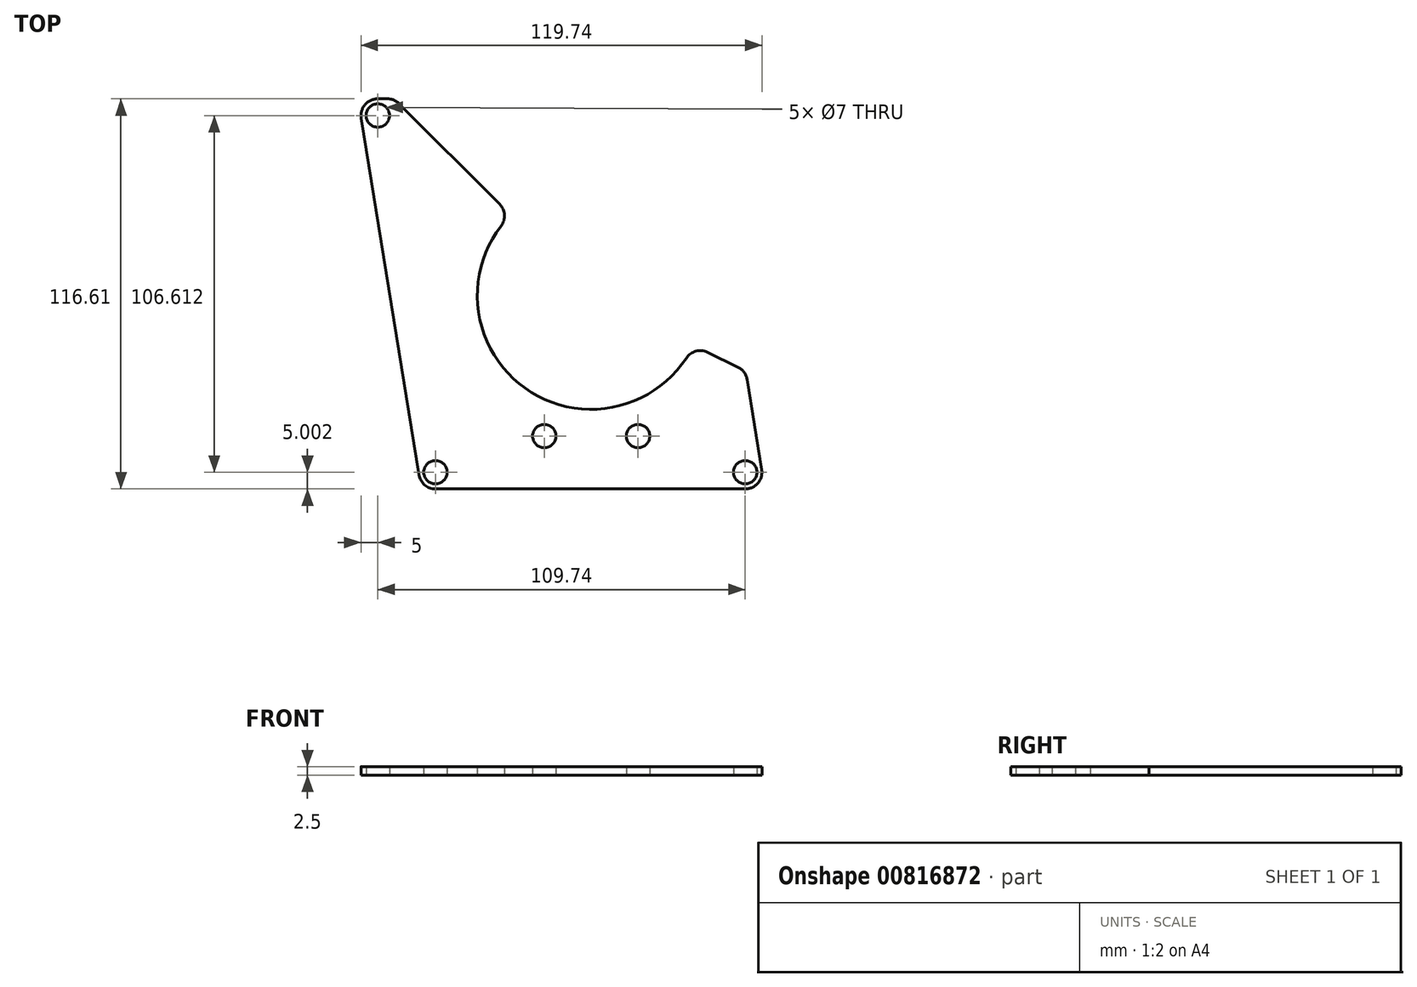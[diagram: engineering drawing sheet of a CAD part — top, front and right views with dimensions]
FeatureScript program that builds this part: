
annotation { "Feature Type Name" : "Feature", "Feature Type Description" : "" }
export const myFeature = defineFeature(function(context is Context, id is Id, definition is map)
    precondition{}
    {
        {
            var Q0;
            Q0=qCreatedBy(makeId("Top.planeOp"),FACE);
            var sketch = newSketch(context, id + "F0", { "sketchPlane" : qUnion([Q0])});
            skLineSegment(sketch, "E0", {"start": v(-63.49, 53.81) * mm, "end": v(29.01, 53.81) * mm, "construction": true});
            skLineSegment(sketch, "E1", {"start": v(-46.25, -52.8) * mm, "end": v(-63.49, 53.81) * mm, "construction": true});
            skLineSegment(sketch, "E2", {"start": v(-46.25, -52.8) * mm, "end": v(46.25, -52.8) * mm, "construction": true});
            skLineSegment(sketch, "E3", {"start": v(29.01, 53.81) * mm, "end": v(46.25, -52.8) * mm, "construction": true});
            skLineSegment(sketch, "E4", {"start": v(-63.49, 58.81) * mm, "end": v(-60.64, 58.81) * mm});
            skLineSegment(sketch, "E5", {"start": v(-51.19, -53.6) * mm, "end": v(-68.43, 53.02) * mm});
            skLineSegment(sketch, "E6", {"start": v(51.19, -52) * mm, "end": v(46.83, -25.08) * mm});
            skLineSegment(sketch, "E7", {"start": v(46.25, -57.8) * mm, "end": v(-46.25, -57.8) * mm});
            skArc(sketch, "E8", {"start": v(-63.49, 58.81) * mm, "mid": v(-67.3, 57.06) * mm, "end": v(-68.43, 53.02) * mm});
            skArc(sketch, "E9", {"start": v(-51.19, -53.6) * mm, "mid": v(-49.5, -56.6) * mm, "end": v(-46.25, -57.8) * mm});
            skArc(sketch, "E10", {"start": v(46.25, -57.8) * mm, "mid": v(50.06, -56.04) * mm, "end": v(51.19, -52) * mm});
            skCircle(sketch, "E11", {"center": v(-63.49, 53.81) * mm, "radius": 3.5 * mm});
            skCircle(sketch, "E12", {"center": v(-46.25, -52.8) * mm, "radius": 3.5 * mm});
            skCircle(sketch, "E13", {"center": v(46.25, -52.8) * mm, "radius": 3.5 * mm});
            skCircle(sketch, "E14", {"center": v(14.25, -42) * mm, "radius": 3.5 * mm});
            skCircle(sketch, "E15", {"center": v(-13.75, -42) * mm, "radius": 3.5 * mm});
            skLineSegment(sketch, "E16", {"start": v(0.25, 21.66) * mm, "end": v(0.25, -33.36) * mm, "construction": true});
            skArc(sketch, "E17", {"start": v(-26.68, 20.76) * mm, "mid": v(-19.5, -27.68) * mm, "end": v(28.65, -18.7) * mm});
            skLineSegment(sketch, "E18", {"start": v(35.01, -16.96) * mm, "end": v(44.09, -21.38) * mm});
            skLineSegment(sketch, "E19", {"start": v(-57.1, 57.35) * mm, "end": v(-27.1, 27.35) * mm});
            skPoint(sketch, "E20.visualSharp", {"position": v(-23.8, 24.04) * mm});
            skArc(sketch, "E20.filletArc", {"start": v(-26.68, 20.76) * mm, "mid": v(-25.65, 24.14) * mm, "end": v(-27.1, 27.35) * mm});
            skPoint(sketch, "E21.visualSharp", {"position": v(30.8, -14.9) * mm});
            skArc(sketch, "E21.filletArc", {"start": v(35.01, -16.96) * mm, "mid": v(31.5, -16.63) * mm, "end": v(28.65, -18.7) * mm});
            skPoint(sketch, "E22.visualSharp", {"position": v(46.42, -22.52) * mm});
            skArc(sketch, "E22.filletArc", {"start": v(46.83, -25.08) * mm, "mid": v(45.91, -22.9) * mm, "end": v(44.09, -21.38) * mm});
            skPoint(sketch, "E23.visualSharp", {"position": v(-58.56, 58.81) * mm});
            skArc(sketch, "E23.filletArc", {"start": v(-57.1, 57.35) * mm, "mid": v(-58.72, 58.43) * mm, "end": v(-60.64, 58.81) * mm});
            skSolve(sketch);
        }
        {
            var Q0;
            Q0 = qSketchRegion(id + "F0", true);
            extrude(context, id + "F1", {"entities" : qUnion([Q0]), "depth" : 2.5 * mm, "offsetDistance" : 25 * mm});
        }
    });
